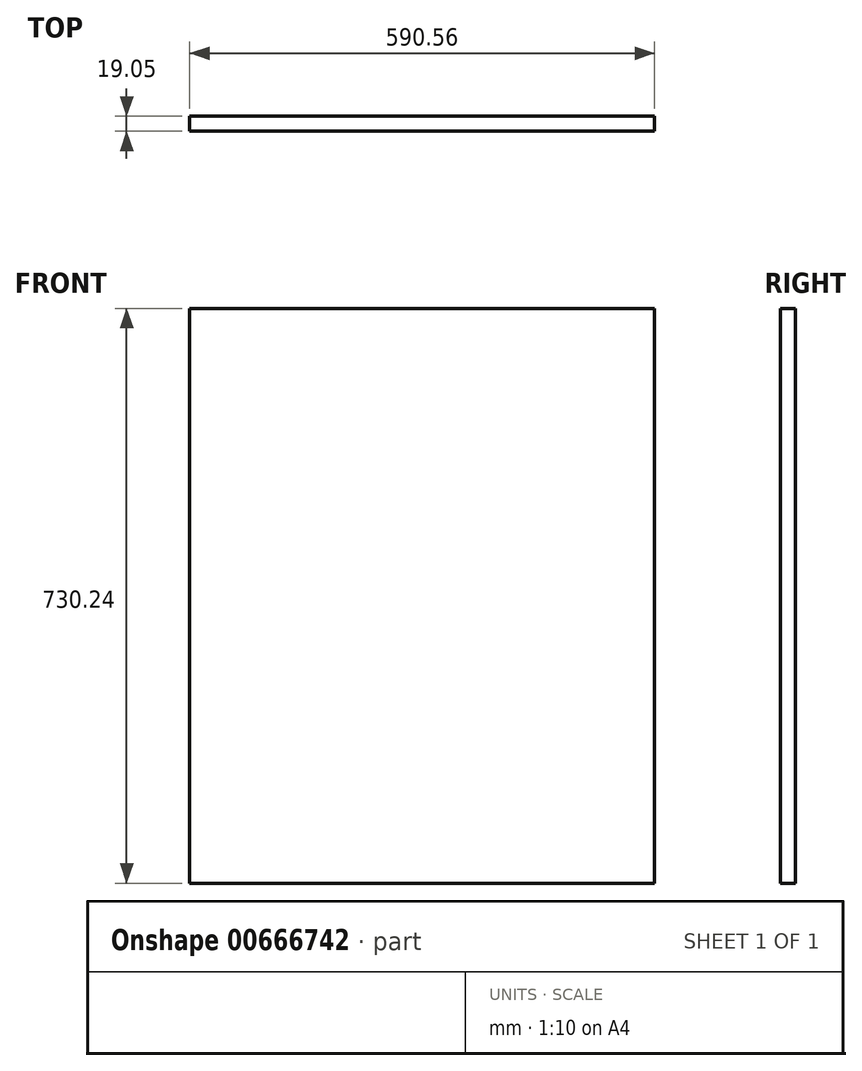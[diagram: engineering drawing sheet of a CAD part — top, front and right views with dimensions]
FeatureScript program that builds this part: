
annotation { "Feature Type Name" : "Feature", "Feature Type Description" : "" }
export const myFeature = defineFeature(function(context is Context, id is Id, definition is map)
    precondition{}
    {
        {
            var Q0;
            Q0=qCreatedBy(makeId("Front.planeOp"),FACE);
            var sketch = newSketch(context, id + "F0", { "sketchPlane" : qUnion([Q0])});
            skLineSegment(sketch, "E0.bottom", {"start": v(295.27, 365.13) * mm, "end": v(-295.28, 365.13) * mm});
            skLineSegment(sketch, "E0.top", {"start": v(295.27, -365.12) * mm, "end": v(-295.28, -365.12) * mm});
            skLineSegment(sketch, "E0.left", {"start": v(295.28, 365.13) * mm, "end": v(295.27, -365.12) * mm});
            skLineSegment(sketch, "E0.right", {"start": v(-295.28, 365.13) * mm, "end": v(-295.28, -365.12) * mm});
            skPoint(sketch, "E0.middle", {"position": v(0, 0) * mm});
            skSolve(sketch);
        }
        {
            var Q0;
            Q0=makeQuery(id+"F0.imprint","IMPRINT",FACE,{"disambiguationData":[TD([[makeQuery(id+"F0.imprint","IMPRINT",EDGE,{"derivedFrom":sQuery(id+"F0.wireOp",EDGE,"E0.bottom")}),1.0]])]});
            extrude(context, id + "F1", {"entities" : qUnion([Q0]), "depth" : 19.05 * mm, "offsetDistance" : 25.4 * mm});
        }
    });
